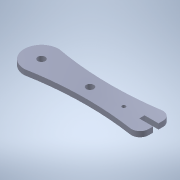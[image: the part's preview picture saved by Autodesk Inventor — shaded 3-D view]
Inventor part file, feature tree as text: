
AUTODESK INVENTOR PART (.ipt)
format: ipt  version: 2020 (Build 240168000, 168)  size: 117,760 bytes
history: mixed  units: mm
features: other x5, extrude x1, sketch x1, reference x1, fillet x1, imported_body x1
ambient origin geometry x8: Origin, YZ Plane, XZ Plane, XY Plane, X Axis, Y Axis, Z Axis, Center Point
bodies: Body1 (imported_parasolid)
feature tree (10):
  other  "Твердое тело1"
  extrude  "Выдавливание1"  Depth=10.0mm TaperAngle=0.0deg
  sketch  "Эскиз1"
  reference  "Ссылка1"
  fillet  "Redondeo2"  [1 undecoded]
  parser-record x1  (decoder bookkeeping rows leaked as tree rows — omitted from the tree; the rows remain in map.json)
  other  "Analisis_brazo.iam"
  other  "Ensamblaje1:1"
  other  "BASE_2.1:1"
  imported_body  NMx_Import_Brep_tag  [imported B-rep: ~15 faces, bbox_mm=[107.0, 5.0, 32.5]]
note: 1 required parameter value undecoded (feature->parameter linkage not recoverable at this tier; creation-order binding heuristic only, values carry confidence <= 0.55)
note: 1 file-system path scrubbed to <path> (originals preserved in map.json)
